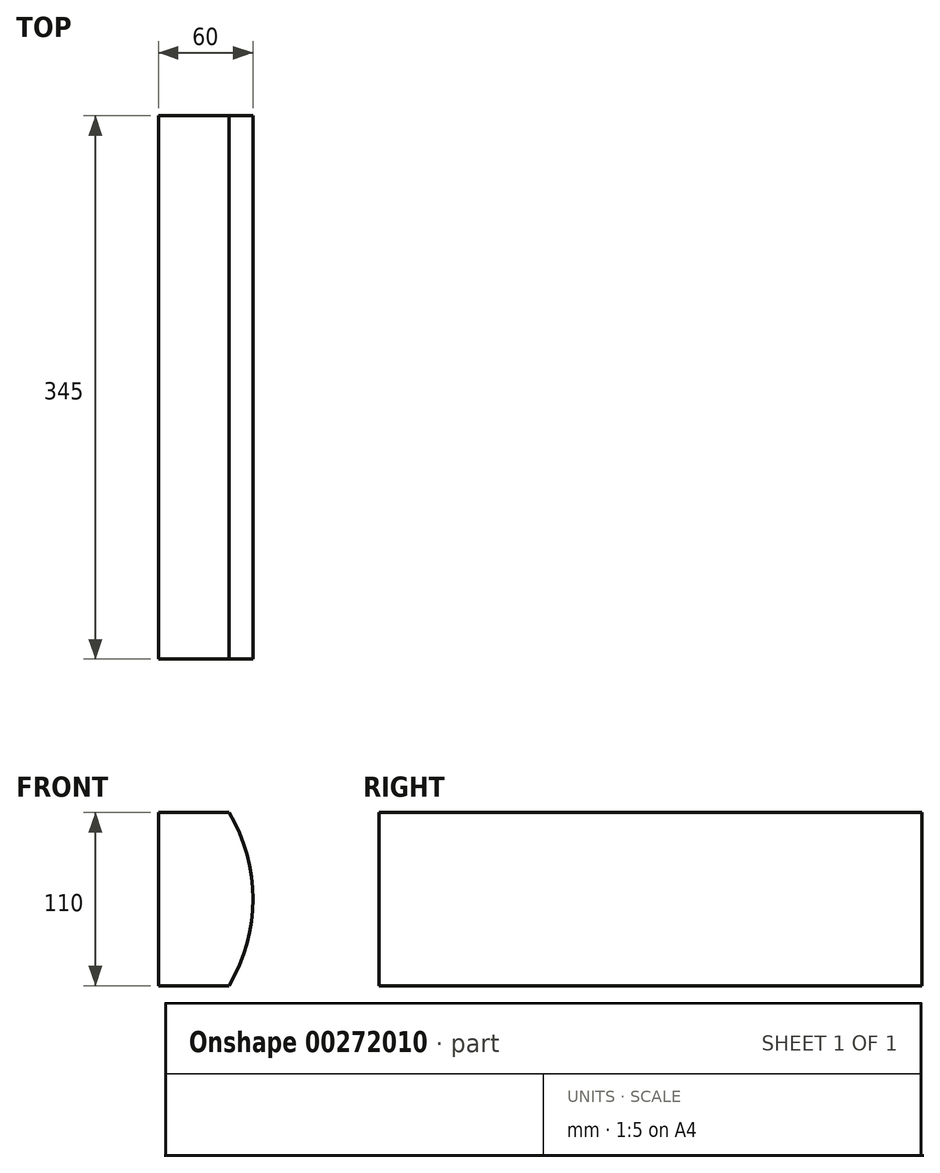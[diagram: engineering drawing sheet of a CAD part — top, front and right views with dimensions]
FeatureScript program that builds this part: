
annotation { "Feature Type Name" : "Feature", "Feature Type Description" : "" }
export const myFeature = defineFeature(function(context is Context, id is Id, definition is map)
    precondition{}
    {
        {
            var Q0;
            Q0=qCreatedBy(makeId("Front.planeOp"),FACE);
            var sketch = newSketch(context, id + "F0", { "sketchPlane" : qUnion([Q0])});
            skLineSegment(sketch, "E0.bottom", {"start": v(0, 0) * mm, "end": v(45, 0) * mm});
            skLineSegment(sketch, "E0.top", {"start": v(0, 110) * mm, "end": v(45, 110) * mm});
            skLineSegment(sketch, "E0.left", {"start": v(0, 0) * mm, "end": v(0, 110) * mm});
            skLineSegment(sketch, "E1", {"start": v(0, 55) * mm, "end": v(60, 55) * mm});
            skArc(sketch, "E2", {"start": v(45, 0) * mm, "mid": v(60, 55) * mm, "end": v(45, 110) * mm});
            skSolve(sketch);
        }
        {
            var Q0;
            {var subQ0=sQuery(id+"F0.wireOp",EDGE,"E0.top");Q0=makeQuery(id+"F0.imprint","IMPRINT",FACE,{"disambiguationData":[TD([[makeQuery(id+"F0.imprint","IMPRINT",EDGE,{"derivedFrom":subQ0}),-1.0]])]});}
            var Q1;
            {var subQ0=sQuery(id+"F0.wireOp",EDGE,"E0.bottom");Q1=makeQuery(id+"F0.imprint","IMPRINT",FACE,{"disambiguationData":[TD([[makeQuery(id+"F0.imprint","IMPRINT",EDGE,{"derivedFrom":subQ0}),1.0]])]});}
            extrude(context, id + "F1", {"entities" : qUnion([Q0, Q1]), "oppositeDirection" : true, "depth" : 345 * mm});
        }
    });
